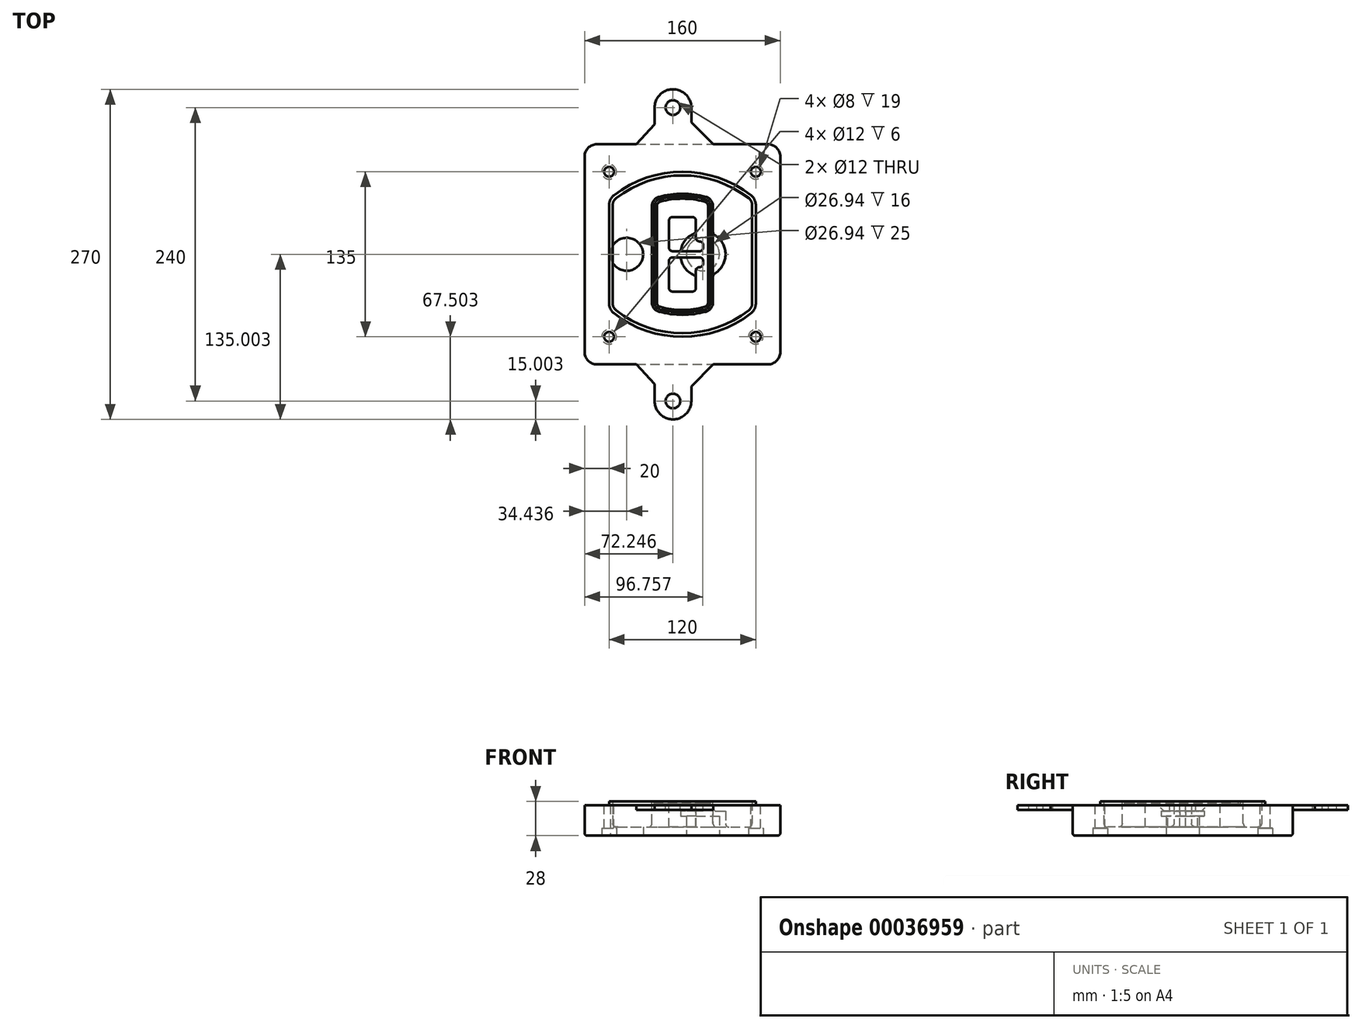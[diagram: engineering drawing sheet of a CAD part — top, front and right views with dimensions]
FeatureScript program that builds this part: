
annotation { "Feature Type Name" : "Feature", "Feature Type Description" : "" }
export const myFeature = defineFeature(function(context is Context, id is Id, definition is map)
    precondition{}
    {
        {
            var Q0;
            Q0=qCreatedBy(makeId("Top.planeOp"),FACE);
            var sketch = newSketch(context, id + "F0", { "sketchPlane" : qUnion([Q0])});
            skPoint(sketch, "E0.rect.middle", {"position": v(0, 0) * mm});
            skLineSegment(sketch, "E1.bottom", {"start": v(24.05, 28.38) * mm, "end": v(164.05, 28.38) * mm});
            skLineSegment(sketch, "E1.top", {"start": v(24.05, 208.38) * mm, "end": v(164.05, 208.38) * mm});
            skLineSegment(sketch, "E1.left", {"start": v(14.05, 38.38) * mm, "end": v(14.05, 198.38) * mm});
            skLineSegment(sketch, "E1.right", {"start": v(174.05, 38.38) * mm, "end": v(174.05, 198.38) * mm});
            skLineSegment(sketch, "E2", {"start": v(14.05, 208.38) * mm, "end": v(174.05, 28.38) * mm, "construction": true});
            skLineSegment(sketch, "E3", {"start": v(174.05, 208.38) * mm, "end": v(14.05, 28.38) * mm, "construction": true});
            skCircle(sketch, "E4", {"center": v(34.05, 185.88) * mm, "radius": 4 * mm});
            skCircle(sketch, "E5", {"center": v(154.05, 185.88) * mm, "radius": 4 * mm});
            skCircle(sketch, "E6", {"center": v(154.05, 50.88) * mm, "radius": 4 * mm});
            skCircle(sketch, "E7", {"center": v(34.05, 50.88) * mm, "radius": 4 * mm});
            skLineSegment(sketch, "E8", {"start": v(34.05, 185.88) * mm, "end": v(154.05, 185.88) * mm, "construction": true});
            skLineSegment(sketch, "E9", {"start": v(154.05, 185.88) * mm, "end": v(154.05, 50.88) * mm, "construction": true});
            skLineSegment(sketch, "E10", {"start": v(154.05, 50.88) * mm, "end": v(34.05, 50.88) * mm, "construction": true});
            skLineSegment(sketch, "E11", {"start": v(34.05, 50.88) * mm, "end": v(34.05, 185.88) * mm, "construction": true});
            skLineSegment(sketch, "E12", {"start": v(34.05, 158.68) * mm, "end": v(34.05, 78.09) * mm});
            skLineSegment(sketch, "E13", {"start": v(154.05, 158.68) * mm, "end": v(154.05, 78.09) * mm});
            skArc(sketch, "E14", {"start": v(150.2, 166.56) * mm, "mid": v(94.05, 185.88) * mm, "end": v(37.9, 166.56) * mm});
            skArc(sketch, "E15", {"start": v(37.9, 70.2) * mm, "mid": v(94.05, 50.88) * mm, "end": v(150.2, 70.2) * mm});
            skLineSegment(sketch, "E16", {"start": v(34.05, 118.38) * mm, "end": v(154.05, 118.38) * mm, "construction": true});
            skPoint(sketch, "E17.visualSharp", {"position": v(34.05, 73.38) * mm});
            skArc(sketch, "E17.filletArc", {"start": v(34.05, 78.09) * mm, "mid": v(35.06, 73.7) * mm, "end": v(37.9, 70.2) * mm});
            skPoint(sketch, "E18.visualSharp", {"position": v(34.05, 163.38) * mm});
            skArc(sketch, "E18.filletArc", {"start": v(37.9, 166.56) * mm, "mid": v(35.06, 163.06) * mm, "end": v(34.05, 158.68) * mm});
            skPoint(sketch, "E19.visualSharp", {"position": v(154.05, 163.38) * mm});
            skArc(sketch, "E19.filletArc", {"start": v(154.05, 158.68) * mm, "mid": v(153.04, 163.06) * mm, "end": v(150.2, 166.56) * mm});
            skPoint(sketch, "E20.visualSharp", {"position": v(154.05, 73.38) * mm});
            skArc(sketch, "E20.filletArc", {"start": v(150.2, 70.2) * mm, "mid": v(153.04, 73.7) * mm, "end": v(154.05, 78.09) * mm});
            skPoint(sketch, "E21.visualSharp", {"position": v(14.05, 208.38) * mm});
            skArc(sketch, "E21.filletArc", {"start": v(24.05, 208.38) * mm, "mid": v(16.98, 205.45) * mm, "end": v(14.05, 198.38) * mm});
            skPoint(sketch, "E22.visualSharp", {"position": v(174.05, 208.38) * mm});
            skArc(sketch, "E22.filletArc", {"start": v(174.05, 198.38) * mm, "mid": v(171.12, 205.45) * mm, "end": v(164.05, 208.38) * mm});
            skPoint(sketch, "E23.visualSharp", {"position": v(174.05, 28.38) * mm});
            skArc(sketch, "E23.filletArc", {"start": v(164.05, 28.38) * mm, "mid": v(171.12, 31.31) * mm, "end": v(174.05, 38.38) * mm});
            skPoint(sketch, "E24.visualSharp", {"position": v(14.05, 28.38) * mm});
            skArc(sketch, "E24.filletArc", {"start": v(14.05, 38.38) * mm, "mid": v(16.98, 31.31) * mm, "end": v(24.05, 28.38) * mm});
            skArc(sketch, "E25.0", {"start": v(151.05, 158.68) * mm, "mid": v(150.34, 161.75) * mm, "end": v(148.36, 164.2) * mm});
            skLineSegment(sketch, "E25.1", {"start": v(151.05, 158.68) * mm, "end": v(151.05, 78.09) * mm});
            skArc(sketch, "E25.2", {"start": v(148.36, 72.57) * mm, "mid": v(150.34, 75.02) * mm, "end": v(151.05, 78.09) * mm});
            skArc(sketch, "E25.3", {"start": v(39.74, 72.57) * mm, "mid": v(94.05, 53.88) * mm, "end": v(148.36, 72.57) * mm});
            skArc(sketch, "E25.4", {"start": v(37.05, 78.09) * mm, "mid": v(37.76, 75.02) * mm, "end": v(39.74, 72.57) * mm});
            skArc(sketch, "E25.5", {"start": v(148.36, 164.2) * mm, "mid": v(94.05, 182.88) * mm, "end": v(39.74, 164.2) * mm});
            skLineSegment(sketch, "E25.6", {"start": v(37.05, 158.68) * mm, "end": v(37.05, 78.09) * mm});
            skArc(sketch, "E25.7", {"start": v(39.74, 164.2) * mm, "mid": v(37.76, 161.75) * mm, "end": v(37.05, 158.68) * mm});
            skArc(sketch, "E26.0", {"start": v(35.43, 169.71) * mm, "mid": v(31.47, 164.82) * mm, "end": v(30.05, 158.68) * mm});
            skArc(sketch, "E26.1", {"start": v(152.67, 169.71) * mm, "mid": v(94.05, 189.88) * mm, "end": v(35.43, 169.71) * mm});
            skArc(sketch, "E26.2", {"start": v(158.05, 158.68) * mm, "mid": v(156.63, 164.82) * mm, "end": v(152.67, 169.71) * mm});
            skLineSegment(sketch, "E26.3", {"start": v(158.05, 158.68) * mm, "end": v(158.05, 78.09) * mm});
            skArc(sketch, "E26.4", {"start": v(152.67, 67.05) * mm, "mid": v(156.63, 71.95) * mm, "end": v(158.05, 78.09) * mm});
            skLineSegment(sketch, "E26.5", {"start": v(30.05, 158.68) * mm, "end": v(30.05, 78.09) * mm});
            skArc(sketch, "E26.6", {"start": v(35.43, 67.05) * mm, "mid": v(94.05, 46.88) * mm, "end": v(152.67, 67.05) * mm});
            skArc(sketch, "E26.7", {"start": v(30.05, 78.09) * mm, "mid": v(31.47, 71.95) * mm, "end": v(35.43, 67.05) * mm});
            skSolve(sketch);
        }
        {
            var Q0;
            Q0=makeQuery(id+"F0.imprint","IMPRINT",FACE,{"disambiguationData":[TD([[makeQuery(id+"F0.imprint","IMPRINT",EDGE,{"derivedFrom":sQuery(id+"F0.wireOp",EDGE,"E1.bottom")}),1.0]])]});
            var Q1;
            Q1=makeQuery(id+"F0.imprint","IMPRINT",FACE,{"disambiguationData":[TD([[makeQuery(id+"F0.imprint","IMPRINT",EDGE,{"derivedFrom":sQuery(id+"F0.wireOp",EDGE,"E12")}),1.0]])]});
            var Q2;
            Q2=makeQuery(id+"F0.imprint","IMPRINT",FACE,{"disambiguationData":[TD([[makeQuery(id+"F0.imprint","IMPRINT",EDGE,{"derivedFrom":sQuery(id+"F0.wireOp",EDGE,"E25.0")}),1.0]])]});
            var Q3;
            Q3=makeQuery(id+"F0.imprint","IMPRINT",FACE,{"disambiguationData":[TD([[makeQuery(id+"F0.imprint","IMPRINT",EDGE,{"derivedFrom":sQuery(id+"F0.wireOp",EDGE,"E12")}),-1.0]])]});
            extrude(context, id + "F1", {"entities" : qUnion([Q0, Q1, Q2, Q3]), "oppositeDirection" : true, "depth" : 25 * mm});
        }
        {
            var Q0;
            Q0=makeQuery(id+"F0.imprint","IMPRINT",FACE,{"disambiguationData":[TD([[makeQuery(id+"F0.imprint","IMPRINT",EDGE,{"derivedFrom":sQuery(id+"F0.wireOp",EDGE,"E12")}),1.0]])]});
            extrude(context, id + "F2", {"entities" : qUnion([Q0]), "operationType" : NewBodyOperationType.ADD, "depth" : 3 * mm});
        }
        {
            var Q0;
            Q0=makeQuery(id+"F0.imprint","IMPRINT",FACE,{"disambiguationData":[TD([[makeQuery(id+"F0.imprint","IMPRINT",EDGE,{"derivedFrom":sQuery(id+"F0.wireOp",EDGE,"E25.0")}),1.0]])]});
            extrude(context, id + "F3", {"entities" : qUnion([Q0]), "operationType" : NewBodyOperationType.REMOVE, "oppositeDirection" : true, "depth" : 18 * mm});
        }
        {
            var Q0;
            Q0=makeQuery(id+"F2.opExtrude","CAP_FACE",FACE,{"disambiguationData":[OSD([sQuery(id+"F0.wireOp",EDGE,"E12"),sQuery(id+"F0.wireOp",EDGE,"E13"),sQuery(id+"F0.wireOp",EDGE,"E14"),sQuery(id+"F0.wireOp",EDGE,"E15"),sQuery(id+"F0.wireOp",EDGE,"E17.filletArc"),sQuery(id+"F0.wireOp",EDGE,"E18.filletArc"),sQuery(id+"F0.wireOp",EDGE,"E19.filletArc"),sQuery(id+"F0.wireOp",EDGE,"E20.filletArc"),sQuery(id+"F0.wireOp",EDGE,"E25.0"),sQuery(id+"F0.wireOp",EDGE,"E25.1"),sQuery(id+"F0.wireOp",EDGE,"E25.2"),sQuery(id+"F0.wireOp",EDGE,"E25.3"),sQuery(id+"F0.wireOp",EDGE,"E25.4"),sQuery(id+"F0.wireOp",EDGE,"E25.5"),sQuery(id+"F0.wireOp",EDGE,"E25.6"),sQuery(id+"F0.wireOp",EDGE,"E25.7")])],"isStart":false});
            var sketch = newSketch(context, id + "F4", { "sketchPlane" : qUnion([Q0])});
            skArc(sketch, "E27.0", {"start": v(74.97, 71.41) * mm, "mid": v(94.05, 68.88) * mm, "end": v(113.13, 71.41) * mm});
            skArc(sketch, "E28.0", {"start": v(113.13, 165.35) * mm, "mid": v(94.05, 167.88) * mm, "end": v(74.97, 165.35) * mm});
            skLineSegment(sketch, "E29", {"start": v(69.05, 157.63) * mm, "end": v(69.05, 79.14) * mm});
            skLineSegment(sketch, "E30", {"start": v(119.05, 157.63) * mm, "end": v(119.05, 79.14) * mm});
            skLineSegment(sketch, "E31", {"start": v(69.05, 163.48) * mm, "end": v(119.05, 163.48) * mm, "construction": true});
            skLineSegment(sketch, "E32", {"start": v(69.05, 73.28) * mm, "end": v(119.05, 73.28) * mm, "construction": true});
            skPoint(sketch, "E33.visualSharp", {"position": v(69.05, 163.48) * mm});
            skArc(sketch, "E33.filletArc", {"start": v(74.97, 165.35) * mm, "mid": v(70.7, 162.5) * mm, "end": v(69.05, 157.63) * mm});
            skPoint(sketch, "E34.visualSharp", {"position": v(119.05, 163.48) * mm});
            skArc(sketch, "E34.filletArc", {"start": v(119.05, 157.63) * mm, "mid": v(117.4, 162.5) * mm, "end": v(113.13, 165.35) * mm});
            skPoint(sketch, "E35.visualSharp", {"position": v(119.05, 73.28) * mm});
            skArc(sketch, "E35.filletArc", {"start": v(113.13, 71.41) * mm, "mid": v(117.4, 74.27) * mm, "end": v(119.05, 79.14) * mm});
            skPoint(sketch, "E36.visualSharp", {"position": v(69.05, 73.28) * mm});
            skArc(sketch, "E36.filletArc", {"start": v(69.05, 79.14) * mm, "mid": v(70.7, 74.27) * mm, "end": v(74.97, 71.41) * mm});
            skArc(sketch, "E37.0", {"start": v(148.36, 164.2) * mm, "mid": v(94.05, 182.88) * mm, "end": v(39.74, 164.2) * mm});
            skArc(sketch, "E37.1", {"start": v(39.74, 164.2) * mm, "mid": v(37.76, 161.75) * mm, "end": v(37.05, 158.68) * mm});
            skLineSegment(sketch, "E37.2", {"start": v(37.05, 158.68) * mm, "end": v(37.05, 78.09) * mm});
            skArc(sketch, "E37.3", {"start": v(37.05, 78.09) * mm, "mid": v(37.76, 75.02) * mm, "end": v(39.74, 72.57) * mm});
            skArc(sketch, "E37.4", {"start": v(39.74, 72.57) * mm, "mid": v(94.05, 53.88) * mm, "end": v(148.36, 72.57) * mm});
            skArc(sketch, "E37.5", {"start": v(148.36, 72.57) * mm, "mid": v(150.34, 75.02) * mm, "end": v(151.05, 78.09) * mm});
            skLineSegment(sketch, "E37.6", {"start": v(151.05, 158.68) * mm, "end": v(151.05, 78.09) * mm});
            skArc(sketch, "E37.7", {"start": v(151.05, 158.68) * mm, "mid": v(150.34, 161.75) * mm, "end": v(148.36, 164.2) * mm});
            skLineSegment(sketch, "E38.0", {"start": v(117.05, 157.63) * mm, "end": v(117.05, 79.14) * mm});
            skArc(sketch, "E38.1", {"start": v(112.61, 73.34) * mm, "mid": v(115.81, 75.49) * mm, "end": v(117.05, 79.14) * mm});
            skArc(sketch, "E38.2", {"start": v(75.49, 73.34) * mm, "mid": v(94.05, 70.88) * mm, "end": v(112.61, 73.34) * mm});
            skArc(sketch, "E38.3", {"start": v(71.05, 79.14) * mm, "mid": v(72.29, 75.49) * mm, "end": v(75.49, 73.34) * mm});
            skLineSegment(sketch, "E38.4", {"start": v(71.05, 157.63) * mm, "end": v(71.05, 79.14) * mm});
            skArc(sketch, "E38.5", {"start": v(117.05, 157.63) * mm, "mid": v(115.81, 161.28) * mm, "end": v(112.61, 163.42) * mm});
            skArc(sketch, "E38.6", {"start": v(75.49, 163.42) * mm, "mid": v(72.29, 161.28) * mm, "end": v(71.05, 157.63) * mm});
            skArc(sketch, "E38.7", {"start": v(112.61, 163.42) * mm, "mid": v(94.05, 165.88) * mm, "end": v(75.49, 163.42) * mm});
            skArc(sketch, "E39.0", {"start": v(115.05, 157.63) * mm, "mid": v(114.23, 160.06) * mm, "end": v(112.1, 161.5) * mm});
            skLineSegment(sketch, "E39.1", {"start": v(115.05, 157.63) * mm, "end": v(115.05, 79.14) * mm});
            skArc(sketch, "E39.2", {"start": v(112.1, 75.27) * mm, "mid": v(114.23, 76.7) * mm, "end": v(115.05, 79.14) * mm});
            skArc(sketch, "E39.3", {"start": v(76, 75.27) * mm, "mid": v(94.05, 72.88) * mm, "end": v(112.1, 75.27) * mm});
            skArc(sketch, "E39.4", {"start": v(73.05, 79.14) * mm, "mid": v(73.87, 76.7) * mm, "end": v(76, 75.27) * mm});
            skArc(sketch, "E39.5", {"start": v(112.1, 161.5) * mm, "mid": v(94.05, 163.88) * mm, "end": v(76, 161.5) * mm});
            skLineSegment(sketch, "E39.6", {"start": v(73.05, 157.63) * mm, "end": v(73.05, 79.14) * mm});
            skArc(sketch, "E39.7", {"start": v(76, 161.5) * mm, "mid": v(73.87, 160.06) * mm, "end": v(73.05, 157.63) * mm});
            skLineSegment(sketch, "E40", {"start": v(69.05, 118.38) * mm, "end": v(119.05, 118.38) * mm, "construction": true});
            skLineSegment(sketch, "E41", {"start": v(83.05, 123.88) * mm, "end": v(83.05, 145.88) * mm});
            skLineSegment(sketch, "E42", {"start": v(86.05, 148.88) * mm, "end": v(102.05, 148.88) * mm});
            skLineSegment(sketch, "E43", {"start": v(105.05, 145.88) * mm, "end": v(105.05, 131.88) * mm});
            skLineSegment(sketch, "E44", {"start": v(108.05, 128.88) * mm, "end": v(108.05, 128.88) * mm});
            skLineSegment(sketch, "E45", {"start": v(111.05, 125.88) * mm, "end": v(111.05, 123.88) * mm});
            skLineSegment(sketch, "E46", {"start": v(108.05, 120.88) * mm, "end": v(86.05, 120.88) * mm});
            skPoint(sketch, "E47.visualSharp", {"position": v(83.05, 148.88) * mm});
            skArc(sketch, "E47.filletArc", {"start": v(86.05, 148.88) * mm, "mid": v(83.93, 148) * mm, "end": v(83.05, 145.88) * mm});
            skPoint(sketch, "E48.visualSharp", {"position": v(105.05, 148.88) * mm});
            skArc(sketch, "E48.filletArc", {"start": v(105.05, 145.88) * mm, "mid": v(104.17, 148) * mm, "end": v(102.05, 148.88) * mm});
            skPoint(sketch, "E49.visualSharp", {"position": v(105.05, 128.88) * mm});
            skArc(sketch, "E49.filletArc", {"start": v(105.05, 131.88) * mm, "mid": v(105.93, 129.76) * mm, "end": v(108.05, 128.88) * mm});
            skPoint(sketch, "E50.visualSharp", {"position": v(111.05, 128.88) * mm});
            skArc(sketch, "E50.filletArc", {"start": v(111.05, 125.88) * mm, "mid": v(110.17, 128) * mm, "end": v(108.05, 128.88) * mm});
            skPoint(sketch, "E51.visualSharp", {"position": v(111.05, 120.88) * mm});
            skArc(sketch, "E51.filletArc", {"start": v(108.05, 120.88) * mm, "mid": v(110.17, 121.76) * mm, "end": v(111.05, 123.88) * mm});
            skPoint(sketch, "E52.visualSharp", {"position": v(83.05, 120.88) * mm});
            skArc(sketch, "E52.filletArc", {"start": v(83.05, 123.88) * mm, "mid": v(83.93, 121.76) * mm, "end": v(86.05, 120.88) * mm});
            skLineSegment(sketch, "E53.0.MirrorCS", {"start": v(108.05, 115.88) * mm, "end": v(86.05, 115.88) * mm});
            skArc(sketch, "E54.0.MirrorCS", {"start": v(83.05, 112.88) * mm, "mid": v(83.93, 115) * mm, "end": v(86.05, 115.88) * mm});
            skLineSegment(sketch, "E55.0.MirrorCS", {"start": v(83.05, 112.88) * mm, "end": v(83.05, 90.88) * mm});
            skArc(sketch, "E56.0.MirrorCS", {"start": v(86.05, 87.88) * mm, "mid": v(83.93, 88.76) * mm, "end": v(83.05, 90.88) * mm});
            skLineSegment(sketch, "E57.0.MirrorCS", {"start": v(86.05, 87.88) * mm, "end": v(102.05, 87.88) * mm});
            skArc(sketch, "E58.0.MirrorCS", {"start": v(105.05, 90.88) * mm, "mid": v(104.17, 88.76) * mm, "end": v(102.05, 87.88) * mm});
            skLineSegment(sketch, "E59.0.MirrorCS", {"start": v(105.05, 90.88) * mm, "end": v(105.05, 104.88) * mm});
            skArc(sketch, "E60.0.MirrorCS", {"start": v(105.05, 104.88) * mm, "mid": v(105.93, 107) * mm, "end": v(108.05, 107.88) * mm});
            skArc(sketch, "E61.0.MirrorCS", {"start": v(111.05, 110.88) * mm, "mid": v(110.17, 108.76) * mm, "end": v(108.05, 107.88) * mm});
            skLineSegment(sketch, "E62.0.MirrorCS", {"start": v(111.05, 110.88) * mm, "end": v(111.05, 112.88) * mm});
            skArc(sketch, "E63.0.MirrorCS", {"start": v(108.05, 115.88) * mm, "mid": v(110.17, 115) * mm, "end": v(111.05, 112.88) * mm});
            skSolve(sketch);
        }
        {
            var Q0;
            Q0=makeQuery(id+"F4.imprint","IMPRINT",FACE,{"disambiguationData":[TD([[makeQuery(id+"F4.imprint","IMPRINT",EDGE,{"derivedFrom":sQuery(id+"F4.wireOp",EDGE,"E27.0")}),1.0]])]});
            var Q1;
            Q1=makeQuery(id+"F4.imprint","IMPRINT",FACE,{"disambiguationData":[TD([[makeQuery(id+"F4.imprint","IMPRINT",EDGE,{"derivedFrom":sQuery(id+"F4.wireOp",EDGE,"E38.0")}),-1.0]])]});
            var Q2;
            Q2=makeQuery(id+"F4.imprint","IMPRINT",FACE,{"disambiguationData":[TD([[makeQuery(id+"F4.imprint","IMPRINT",EDGE,{"derivedFrom":sQuery(id+"F4.wireOp",EDGE,"E39.0")}),1.0]])]});
            extrude(context, id + "F5", {"entities" : qUnion([Q0, Q1, Q2]), "operationType" : NewBodyOperationType.ADD, "endBound" : BoundingType.UP_TO_NEXT, "oppositeDirection" : true, "depth" : 25 * mm});
        }
        {
            var Q0;
            Q0=makeQuery(id+"F4.imprint","IMPRINT",FACE,{"disambiguationData":[TD([[makeQuery(id+"F4.imprint","IMPRINT",EDGE,{"derivedFrom":sQuery(id+"F4.wireOp",EDGE,"E38.0")}),-1.0]])]});
            extrude(context, id + "F6", {"entities" : qUnion([Q0]), "operationType" : NewBodyOperationType.REMOVE, "oppositeDirection" : true, "depth" : 2 * mm});
        }
        {
            var Q0;
            Q0=makeQuery(id+"F1.opExtrude","CAP_FACE",FACE,{"disambiguationData":[OSD([sQuery(id+"F0.wireOp",EDGE,"E1.bottom"),sQuery(id+"F0.wireOp",EDGE,"E1.top"),sQuery(id+"F0.wireOp",EDGE,"E1.left"),sQuery(id+"F0.wireOp",EDGE,"E1.right"),sQuery(id+"F0.wireOp",EDGE,"E4"),sQuery(id+"F0.wireOp",EDGE,"E5"),sQuery(id+"F0.wireOp",EDGE,"E6"),sQuery(id+"F0.wireOp",EDGE,"E7"),sQuery(id+"F0.wireOp",EDGE,"E21.filletArc"),sQuery(id+"F0.wireOp",EDGE,"E22.filletArc"),sQuery(id+"F0.wireOp",EDGE,"E23.filletArc"),sQuery(id+"F0.wireOp",EDGE,"E24.filletArc")])],"isStart":false});
            var sketch = newSketch(context, id + "F7", { "sketchPlane" : qUnion([Q0])});
            skCircle(sketch, "E64", {"center": v(110.8, -118.38) * mm, "radius": 13.47 * mm});
            skCircle(sketch, "E65", {"center": v(48.49, -118.38) * mm, "radius": 13.47 * mm});
            skLineSegment(sketch, "E66", {"start": v(174.05, -118.38) * mm, "end": v(14.05, -118.38) * mm});
            skCircle(sketch, "E67", {"center": v(110.8, -118.38) * mm, "radius": 18.47 * mm});
            skCircle(sketch, "E68", {"center": v(154.05, -185.88) * mm, "radius": 6 * mm});
            skCircle(sketch, "E69", {"center": v(34.05, -185.88) * mm, "radius": 6 * mm});
            skCircle(sketch, "E70", {"center": v(34.05, -50.88) * mm, "radius": 6 * mm});
            skCircle(sketch, "E71", {"center": v(154.05, -50.88) * mm, "radius": 6 * mm});
            skSolve(sketch);
        }
        {
            var Q0;
            {var subQ1=sQuery(id+"F7.wireOp",EDGE,"E66");var subQ4=sQuery(id+"F7.wireOp",EDGE,"E64");var subQ6=makeQuery(id+"F7.imprint","INTERSECT",VERTEX,{"disambiguationData":[OD(0.0)],"derivedFrom":[subQ4,subQ1]});Q0=makeQuery(id+"F7.imprint","IMPRINT",FACE,{"disambiguationData":[TD([[makeQuery(id+"F7.imprint","IMPRINT",EDGE,{"disambiguationData":[TD([[subQ6,-1.0]])],"derivedFrom":subQ4}),-1.0]])]});}
            var Q1;
            {var subQ0=sQuery(id+"F7.wireOp",EDGE,"E66");var subQ1=sQuery(id+"F7.wireOp",EDGE,"E64");var subQ3=makeQuery(id+"F7.imprint","INTERSECT",VERTEX,{"disambiguationData":[OD(0.0)],"derivedFrom":[subQ1,subQ0]});Q1=makeQuery(id+"F7.imprint","IMPRINT",FACE,{"disambiguationData":[TD([[makeQuery(id+"F7.imprint","IMPRINT",EDGE,{"disambiguationData":[TD([[subQ3,-1.0]])],"derivedFrom":subQ1}),1.0]])]});}
            var Q2;
            {var subQ0=sQuery(id+"F7.wireOp",EDGE,"E66");var subQ1=sQuery(id+"F7.wireOp",EDGE,"E64");var subQ3=makeQuery(id+"F7.imprint","INTERSECT",VERTEX,{"disambiguationData":[OD(0.0)],"derivedFrom":[subQ1,subQ0]});Q2=makeQuery(id+"F7.imprint","IMPRINT",FACE,{"disambiguationData":[TD([[makeQuery(id+"F7.imprint","IMPRINT",EDGE,{"disambiguationData":[TD([[subQ3,1.0]])],"derivedFrom":subQ1}),1.0]])]});}
            var Q3;
            {var subQ1=sQuery(id+"F7.wireOp",EDGE,"E66");var subQ4=sQuery(id+"F7.wireOp",EDGE,"E64");var subQ6=makeQuery(id+"F7.imprint","INTERSECT",VERTEX,{"disambiguationData":[OD(0.0)],"derivedFrom":[subQ4,subQ1]});Q3=makeQuery(id+"F7.imprint","IMPRINT",FACE,{"disambiguationData":[TD([[makeQuery(id+"F7.imprint","IMPRINT",EDGE,{"disambiguationData":[TD([[subQ6,1.0]])],"derivedFrom":subQ4}),-1.0]])]});}
            extrude(context, id + "F8", {"entities" : qUnion([Q0, Q1, Q2, Q3]), "operationType" : NewBodyOperationType.ADD, "oppositeDirection" : true, "depth" : 20 * mm});
        }
        {
            var Q0;
            {var subQ0=sQuery(id+"F7.wireOp",EDGE,"E66");var subQ1=sQuery(id+"F7.wireOp",EDGE,"E64");var subQ3=makeQuery(id+"F7.imprint","INTERSECT",VERTEX,{"disambiguationData":[OD(0.0)],"derivedFrom":[subQ1,subQ0]});Q0=makeQuery(id+"F7.imprint","IMPRINT",FACE,{"disambiguationData":[TD([[makeQuery(id+"F7.imprint","IMPRINT",EDGE,{"disambiguationData":[TD([[subQ3,-1.0]])],"derivedFrom":subQ1}),1.0]])]});}
            var Q1;
            {var subQ0=sQuery(id+"F7.wireOp",EDGE,"E66");var subQ1=sQuery(id+"F7.wireOp",EDGE,"E64");var subQ3=makeQuery(id+"F7.imprint","INTERSECT",VERTEX,{"disambiguationData":[OD(0.0)],"derivedFrom":[subQ1,subQ0]});Q1=makeQuery(id+"F7.imprint","IMPRINT",FACE,{"disambiguationData":[TD([[makeQuery(id+"F7.imprint","IMPRINT",EDGE,{"disambiguationData":[TD([[subQ3,1.0]])],"derivedFrom":subQ1}),1.0]])]});}
            extrude(context, id + "F9", {"entities" : qUnion([Q0, Q1]), "operationType" : NewBodyOperationType.REMOVE, "oppositeDirection" : true, "depth" : 16 * mm});
        }
        {
            var Q0;
            {var subQ0=sQuery(id+"F7.wireOp",EDGE,"E66");var subQ1=sQuery(id+"F7.wireOp",EDGE,"E65");var subQ3=makeQuery(id+"F7.imprint","INTERSECT",VERTEX,{"disambiguationData":[OD(0.0)],"derivedFrom":[subQ1,subQ0]});Q0=makeQuery(id+"F7.imprint","IMPRINT",FACE,{"disambiguationData":[TD([[makeQuery(id+"F7.imprint","IMPRINT",EDGE,{"disambiguationData":[TD([[subQ3,-1.0]])],"derivedFrom":subQ1}),1.0]])]});}
            var Q1;
            {var subQ0=sQuery(id+"F7.wireOp",EDGE,"E66");var subQ1=sQuery(id+"F7.wireOp",EDGE,"E65");var subQ3=makeQuery(id+"F7.imprint","INTERSECT",VERTEX,{"disambiguationData":[OD(0.0)],"derivedFrom":[subQ1,subQ0]});Q1=makeQuery(id+"F7.imprint","IMPRINT",FACE,{"disambiguationData":[TD([[makeQuery(id+"F7.imprint","IMPRINT",EDGE,{"disambiguationData":[TD([[subQ3,1.0]])],"derivedFrom":subQ1}),1.0]])]});}
            extrude(context, id + "F10", {"entities" : qUnion([Q0, Q1]), "operationType" : NewBodyOperationType.REMOVE, "oppositeDirection" : true, "depth" : 25 * mm});
        }
        {
            var Q0;
            Q0=makeQuery(id+"F7.imprint","IMPRINT",FACE,{"disambiguationData":[TD([[makeQuery(id+"F7.imprint","IMPRINT",EDGE,{"derivedFrom":sQuery(id+"F7.wireOp",EDGE,"E68")}),1.0]])]});
            var Q1;
            Q1=makeQuery(id+"F7.imprint","IMPRINT",FACE,{"disambiguationData":[TD([[makeQuery(id+"F7.imprint","IMPRINT",EDGE,{"derivedFrom":makeQuery(id+"F1.opExtrude","CAP_EDGE",EDGE,{"disambiguationData":[OSD([sQuery(id+"F0.wireOp",EDGE,"E5")])],"isStart":false})}),-1.0]])]});
            var Q2;
            Q2=makeQuery(id+"F7.imprint","IMPRINT",FACE,{"disambiguationData":[TD([[makeQuery(id+"F7.imprint","IMPRINT",EDGE,{"derivedFrom":sQuery(id+"F7.wireOp",EDGE,"E69")}),1.0]])]});
            var Q3;
            Q3=makeQuery(id+"F7.imprint","IMPRINT",FACE,{"disambiguationData":[TD([[makeQuery(id+"F7.imprint","IMPRINT",EDGE,{"derivedFrom":makeQuery(id+"F1.opExtrude","CAP_EDGE",EDGE,{"disambiguationData":[OSD([sQuery(id+"F0.wireOp",EDGE,"E4")])],"isStart":false})}),-1.0]])]});
            var Q4;
            Q4=makeQuery(id+"F7.imprint","IMPRINT",FACE,{"disambiguationData":[TD([[makeQuery(id+"F7.imprint","IMPRINT",EDGE,{"derivedFrom":sQuery(id+"F7.wireOp",EDGE,"E70")}),1.0]])]});
            var Q5;
            Q5=makeQuery(id+"F7.imprint","IMPRINT",FACE,{"disambiguationData":[TD([[makeQuery(id+"F7.imprint","IMPRINT",EDGE,{"derivedFrom":makeQuery(id+"F1.opExtrude","CAP_EDGE",EDGE,{"disambiguationData":[OSD([sQuery(id+"F0.wireOp",EDGE,"E7")])],"isStart":false})}),-1.0]])]});
            var Q6;
            Q6=makeQuery(id+"F7.imprint","IMPRINT",FACE,{"disambiguationData":[TD([[makeQuery(id+"F7.imprint","IMPRINT",EDGE,{"derivedFrom":sQuery(id+"F7.wireOp",EDGE,"E71")}),1.0]])]});
            var Q7;
            Q7=makeQuery(id+"F7.imprint","IMPRINT",FACE,{"disambiguationData":[TD([[makeQuery(id+"F7.imprint","IMPRINT",EDGE,{"derivedFrom":makeQuery(id+"F1.opExtrude","CAP_EDGE",EDGE,{"disambiguationData":[OSD([sQuery(id+"F0.wireOp",EDGE,"E6")])],"isStart":false})}),-1.0]])]});
            extrude(context, id + "F11", {"entities" : qUnion([Q0, Q1, Q2, Q3, Q4, Q5, Q6, Q7]), "operationType" : NewBodyOperationType.REMOVE, "oppositeDirection" : true, "depth" : 6 * mm});
        }
        {
            var Q0;
            Q0=makeQuery(id+"F9.boolean.opBoolean","COPY",FACE,{"derivedFrom":makeQuery(id+"F9.opExtrude","CAP_FACE",FACE,{"disambiguationData":[OSD([sQuery(id+"F7.wireOp",EDGE,"E64")])],"isStart":false})});
            var sketch = newSketch(context, id + "F12", { "sketchPlane" : qUnion([Q0])});
            skArc(sketch, "E72.0", {"start": v(105.05, -100.83) * mm, "mid": v(96.62, -106.56) * mm, "end": v(92.5, -115.88) * mm});
            skArc(sketch, "E72.1", {"start": v(92.5, -120.88) * mm, "mid": v(96.62, -130.2) * mm, "end": v(105.05, -135.93) * mm});
            skLineSegment(sketch, "E73", {"start": v(92.5, -120.88) * mm, "end": v(108.05, -120.88) * mm});
            skLineSegment(sketch, "E74.0", {"start": v(108.05, -115.88) * mm, "end": v(92.5, -115.88) * mm});
            skArc(sketch, "E74.1", {"start": v(108.05, -115.88) * mm, "mid": v(110.17, -115) * mm, "end": v(111.05, -112.88) * mm});
            skLineSegment(sketch, "E74.2", {"start": v(111.05, -110.88) * mm, "end": v(111.05, -112.88) * mm});
            skArc(sketch, "E74.3", {"start": v(111.05, -110.88) * mm, "mid": v(110.17, -108.76) * mm, "end": v(108.05, -107.88) * mm});
            skArc(sketch, "E74.4", {"start": v(105.05, -104.88) * mm, "mid": v(105.93, -107) * mm, "end": v(108.05, -107.88) * mm});
            skLineSegment(sketch, "E74.5", {"start": v(105.05, -100.83) * mm, "end": v(105.05, -104.88) * mm});
            skLineSegment(sketch, "E74.7", {"start": v(108.05, -120.88) * mm, "end": v(92.5, -120.88) * mm});
            skArc(sketch, "E74.8", {"start": v(108.05, -120.88) * mm, "mid": v(110.17, -121.76) * mm, "end": v(111.05, -123.88) * mm});
            skLineSegment(sketch, "E74.9", {"start": v(111.05, -125.88) * mm, "end": v(111.05, -123.88) * mm});
            skArc(sketch, "E74.10", {"start": v(111.05, -125.88) * mm, "mid": v(110.17, -128) * mm, "end": v(108.05, -128.88) * mm});
            skArc(sketch, "E74.11", {"start": v(105.05, -131.88) * mm, "mid": v(105.93, -129.76) * mm, "end": v(108.05, -128.88) * mm});
            skLineSegment(sketch, "E74.12", {"start": v(105.05, -135.93) * mm, "end": v(105.05, -131.88) * mm});
            skPoint(sketch, "E75.orphan", {"position": v(105.05, -145.88) * mm});
            skPoint(sketch, "E76.orphan", {"position": v(86.05, -120.88) * mm});
            skPoint(sketch, "E77.orphan", {"position": v(86.05, -115.88) * mm});
            skPoint(sketch, "E78.orphan", {"position": v(105.05, -90.88) * mm});
            skSolve(sketch);
        }
        {
            var Q0;
            {var subQ7=sQuery(id+"F12.wireOp",EDGE,"E72.0");var subQ14=sQuery(id+"F12.wireOp",EDGE,"E72.1");var subQ16=sQuery(id+"F12.wireOp",EDGE,"E74.1");var subQ18=sQuery(id+"F12.wireOp",EDGE,"E74.8");Q0=qUnion([makeQuery(id+"F12.imprint","IMPRINT",FACE,{"disambiguationData":[TD([[makeQuery(id+"F12.imprint","IMPRINT",EDGE,{"derivedFrom":subQ7}),1.0]])]}),makeQuery(id+"F12.imprint","IMPRINT",FACE,{"disambiguationData":[TD([[makeQuery(id+"F12.imprint","IMPRINT",EDGE,{"derivedFrom":subQ14}),1.0]])]}),makeQuery(id+"F12.imprint","IMPRINT",FACE,{"disambiguationData":[TD([[makeQuery(id+"F12.imprint","IMPRINT",EDGE,{"derivedFrom":subQ16}),1.0]])]}),makeQuery(id+"F12.imprint","IMPRINT",FACE,{"disambiguationData":[TD([[makeQuery(id+"F12.imprint","IMPRINT",EDGE,{"derivedFrom":subQ18}),-1.0]])]})]);}
            var Q1;
            Q1=makeQuery(id+"F5.boolean.opBoolean","SPLIT",FACE,{"disambiguationData":[TD([makeQuery(id+"F5.opExtrude","SWEPT_FACE",FACE,{"disambiguationData":[OSD([sQuery(id+"F4.wireOp",EDGE,"E41")])]})])],"derivedFrom":makeQuery(id+"F3.boolean.opBoolean","COPY",FACE,{"derivedFrom":makeQuery(id+"F3.opExtrude","CAP_FACE",FACE,{"disambiguationData":[OSD([sQuery(id+"F0.wireOp",EDGE,"E25.0"),sQuery(id+"F0.wireOp",EDGE,"E25.1"),sQuery(id+"F0.wireOp",EDGE,"E25.2"),sQuery(id+"F0.wireOp",EDGE,"E25.3"),sQuery(id+"F0.wireOp",EDGE,"E25.4"),sQuery(id+"F0.wireOp",EDGE,"E25.5"),sQuery(id+"F0.wireOp",EDGE,"E25.6"),sQuery(id+"F0.wireOp",EDGE,"E25.7")])],"isStart":false})})});
            extrude(context, id + "F13", {"entities" : qUnion([Q0]), "operationType" : NewBodyOperationType.REMOVE, "endBound" : BoundingType.UP_TO_SURFACE, "endBoundEntityFace" : qUnion([Q1]), "depth" : 25 * mm});
        }
        {
            var Q0;
            Q0=makeQuery(id+"F3.boolean.opBoolean","COPY",EDGE,{"derivedFrom":makeQuery(id+"F3.opExtrude","CAP_EDGE",EDGE,{"disambiguationData":[OSD([sQuery(id+"F0.wireOp",EDGE,"E25.6")])],"isStart":false})});
            var Q1;
            Q1=makeQuery(id+"F8.boolean.opBoolean","INTERSECT",EDGE,{"derivedFrom":[makeQuery(id+"F5.opExtrude","SWEPT_FACE",FACE,{"disambiguationData":[OSD([sQuery(id+"F4.wireOp",EDGE,"E30")])]}),makeQuery(id+"F8.opExtrude","CAP_FACE",FACE,{"disambiguationData":[OSD([sQuery(id+"F7.wireOp",EDGE,"E67")])],"isStart":false})]});
            var Q2;
            Q2=makeQuery(id+"F8.boolean.opBoolean","INTERSECT",EDGE,{"disambiguationData":[OD(1.0)],"derivedFrom":[makeQuery(id+"F5.opExtrude","SWEPT_FACE",FACE,{"disambiguationData":[OSD([sQuery(id+"F4.wireOp",EDGE,"E30")])]}),makeQuery(id+"F8.opExtrude","SWEPT_FACE",FACE,{"disambiguationData":[OSD([sQuery(id+"F7.wireOp",EDGE,"E67")])]})]});
            var Q3;
            {var subQ0=sQuery(id+"F4.wireOp",EDGE,"E30");Q3=makeQuery(id+"F8.boolean.opBoolean","SPLIT",EDGE,{"disambiguationData":[TD([makeQuery(id+"F5.opExtrude","SWEPT_FACE",FACE,{"disambiguationData":[OSD([sQuery(id+"F4.wireOp",EDGE,"E35.filletArc")])]})])],"derivedFrom":makeQuery(id+"F5.opExtrude","CAP_EDGE",EDGE,{"disambiguationData":[OSD([subQ0])],"isStart":false})});}
            var Q4;
            {var subQ0=sQuery(id+"F0.wireOp",EDGE,"E25.7");var subQ1=sQuery(id+"F0.wireOp",EDGE,"E25.1");var subQ2=sQuery(id+"F0.wireOp",EDGE,"E25.6");var subQ3=sQuery(id+"F0.wireOp",EDGE,"E25.5");var subQ4=sQuery(id+"F0.wireOp",EDGE,"E25.4");var subQ5=sQuery(id+"F0.wireOp",EDGE,"E25.0");var subQ6=sQuery(id+"F0.wireOp",EDGE,"E25.2");var subQ7=sQuery(id+"F0.wireOp",EDGE,"E25.3");Q4=makeQuery(id+"F8.boolean.opBoolean","INTERSECT",EDGE,{"derivedFrom":[makeQuery(id+"F5.boolean.opBoolean","SPLIT",FACE,{"disambiguationData":[TD([makeQuery(id+"F2.opExtrude","SWEPT_FACE",FACE,{"disambiguationData":[OSD([subQ5])]})])],"derivedFrom":makeQuery(id+"F3.boolean.opBoolean","COPY",FACE,{"derivedFrom":makeQuery(id+"F3.opExtrude","CAP_FACE",FACE,{"disambiguationData":[OSD([subQ5,subQ1,subQ6,subQ7,subQ4,subQ3,subQ2,subQ0])],"isStart":false})})}),makeQuery(id+"F8.opExtrude","SWEPT_FACE",FACE,{"disambiguationData":[OSD([sQuery(id+"F7.wireOp",EDGE,"E67")])]})]});}
            var Q5;
            Q5=makeQuery(id+"F8.boolean.opBoolean","INTERSECT",EDGE,{"disambiguationData":[OD(0.0)],"derivedFrom":[makeQuery(id+"F5.opExtrude","SWEPT_FACE",FACE,{"disambiguationData":[OSD([sQuery(id+"F4.wireOp",EDGE,"E30")])]}),makeQuery(id+"F8.opExtrude","SWEPT_FACE",FACE,{"disambiguationData":[OSD([sQuery(id+"F7.wireOp",EDGE,"E67")])]})]});
            fillet(context, id + "F14", {"entities" : qUnion([Q0, Q1, Q2, Q3, Q4, Q5]), "radius" : 3 * mm, "tangentPropagation" : true, "allowEdgeOverflow" : false});
        }
        {
            var Q0;
            Q0=makeQuery(id+"F1.opExtrude","CAP_EDGE",EDGE,{"disambiguationData":[OSD([sQuery(id+"F0.wireOp",EDGE,"E1.bottom")])],"isStart":false});
            fillet(context, id + "F15", {"entities" : qUnion([Q0]), "radius" : 2 * mm, "tangentPropagation" : true, "allowEdgeOverflow" : false});
        }
        {
            var Q0;
            {var subQ0=sQuery(id+"F0.wireOp",EDGE,"E1.bottom");var subQ1=sQuery(id+"F0.wireOp",EDGE,"E1.top");var subQ2=sQuery(id+"F0.wireOp",EDGE,"E1.left");var subQ3=sQuery(id+"F0.wireOp",EDGE,"E1.right");var subQ4=sQuery(id+"F0.wireOp",EDGE,"E4");var subQ5=sQuery(id+"F0.wireOp",EDGE,"E5");var subQ6=sQuery(id+"F0.wireOp",EDGE,"E6");var subQ7=sQuery(id+"F0.wireOp",EDGE,"E7");var subQ8=sQuery(id+"F0.wireOp",EDGE,"E21.filletArc");var subQ9=sQuery(id+"F0.wireOp",EDGE,"E22.filletArc");var subQ10=sQuery(id+"F0.wireOp",EDGE,"E23.filletArc");var subQ11=sQuery(id+"F0.wireOp",EDGE,"E24.filletArc");Q0=makeQuery(id+"F2.boolean.opBoolean","SPLIT",FACE,{"disambiguationData":[TD([makeQuery(id+"F1.opExtrude","SWEPT_FACE",FACE,{"disambiguationData":[OSD([subQ0])]})])],"derivedFrom":makeQuery(id+"F1.opExtrude","CAP_FACE",FACE,{"disambiguationData":[OSD([subQ0,subQ1,subQ2,subQ3,subQ4,subQ5,subQ6,subQ7,subQ8,subQ9,subQ10,subQ11])],"isStart":true})});}
            var sketch = newSketch(context, id + "F16", { "sketchPlane" : qUnion([Q0])});
            skLineSegment(sketch, "E79", {"start": v(56.4, 208.38) * mm, "end": v(71.31, 224.6) * mm});
            skLineSegment(sketch, "E80", {"start": v(71.31, 224.6) * mm, "end": v(71.31, 237.7) * mm});
            skLineSegment(sketch, "E81", {"start": v(101.3, 226.38) * mm, "end": v(119.3, 208.38) * mm});
            skLineSegment(sketch, "E82", {"start": v(119.3, 208.38) * mm, "end": v(101.3, 226.38) * mm});
            skLineSegment(sketch, "E83", {"start": v(101.3, 238.38) * mm, "end": v(101.3, 226.38) * mm});
            skArc(sketch, "E84", {"start": v(101.3, 238.38) * mm, "mid": v(85.95, 253.38) * mm, "end": v(71.31, 237.7) * mm});
            skLineSegment(sketch, "E85", {"start": v(86.3, 238.38) * mm, "end": v(86.3, 208.38) * mm, "construction": true});
            skCircle(sketch, "E86", {"center": v(86.3, 238.38) * mm, "radius": 6 * mm});
            skLineSegment(sketch, "E87", {"start": v(14.05, 118.38) * mm, "end": v(174.05, 118.38) * mm, "construction": true});
            skLineSegment(sketch, "E88.MirrorCS", {"start": v(56.4, 28.38) * mm, "end": v(71.31, 12.16) * mm});
            skLineSegment(sketch, "E89.MirrorCS", {"start": v(71.31, 12.16) * mm, "end": v(71.31, -0.94) * mm});
            skArc(sketch, "E90.MirrorCS", {"start": v(101.3, -1.62) * mm, "mid": v(85.95, -16.61) * mm, "end": v(71.31, -0.94) * mm});
            skCircle(sketch, "E91.MirrorC", {"center": v(86.3, -1.62) * mm, "radius": 6 * mm});
            skLineSegment(sketch, "E92.MirrorCS", {"start": v(86.3, -1.62) * mm, "end": v(86.3, 28.38) * mm});
            skLineSegment(sketch, "E93.MirrorCS", {"start": v(119.3, 28.38) * mm, "end": v(101.3, 10.38) * mm});
            skLineSegment(sketch, "E94.MirrorCS", {"start": v(101.3, -1.62) * mm, "end": v(101.3, 10.38) * mm});
            skSolve(sketch);
        }
        {
            var Q0;
            {var subQ1=sQuery(id+"F16.wireOp",EDGE,"E88.MirrorCS");Q0=makeQuery(id+"F16.imprint","IMPRINT",FACE,{"disambiguationData":[TD([[makeQuery(id+"F16.imprint","IMPRINT",EDGE,{"derivedFrom":subQ1}),1.0]])]});}
            var Q1;
            {var subQ2=sQuery(id+"F16.wireOp",EDGE,"E79");Q1=makeQuery(id+"F16.imprint","IMPRINT",FACE,{"disambiguationData":[TD([[makeQuery(id+"F16.imprint","IMPRINT",EDGE,{"derivedFrom":subQ2}),-1.0]])]});}
            var Q2;
            Q2 = qConstructionFilter(qBodyType(qCreatedBy(id + "F16" ,EDGE), BodyType.WIRE), ConstructionObject.NO);
            var Q3;
            {var subQ0=sQuery(id+"F0.wireOp",EDGE,"E1.bottom");var subQ1=sQuery(id+"F0.wireOp",EDGE,"E1.top");var subQ2=sQuery(id+"F0.wireOp",EDGE,"E1.left");var subQ3=sQuery(id+"F0.wireOp",EDGE,"E1.right");var subQ4=sQuery(id+"F0.wireOp",EDGE,"E4");var subQ5=sQuery(id+"F0.wireOp",EDGE,"E5");var subQ6=sQuery(id+"F0.wireOp",EDGE,"E6");var subQ7=sQuery(id+"F0.wireOp",EDGE,"E7");var subQ8=sQuery(id+"F0.wireOp",EDGE,"E21.filletArc");var subQ9=sQuery(id+"F0.wireOp",EDGE,"E22.filletArc");var subQ10=sQuery(id+"F0.wireOp",EDGE,"E23.filletArc");var subQ11=sQuery(id+"F0.wireOp",EDGE,"E24.filletArc");Q3=makeQuery(id+"F2.boolean.opBoolean","SPLIT",FACE,{"disambiguationData":[TD([makeQuery(id+"F1.opExtrude","SWEPT_FACE",FACE,{"disambiguationData":[OSD([subQ0])]})])],"derivedFrom":makeQuery(id+"F1.opExtrude","CAP_FACE",FACE,{"disambiguationData":[OSD([subQ0,subQ1,subQ2,subQ3,subQ4,subQ5,subQ6,subQ7,subQ8,subQ9,subQ10,subQ11])],"isStart":true})});}
            extrude(context, id + "F17", {"entities" : qUnion([Q0, Q1]), "operationType" : NewBodyOperationType.ADD, "surfaceEntities" : qUnion([Q2]), "oppositeDirection" : true, "endBoundEntityFace" : qUnion([Q3]), "depth" : 4 * mm});
        }
    });
